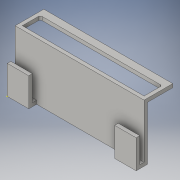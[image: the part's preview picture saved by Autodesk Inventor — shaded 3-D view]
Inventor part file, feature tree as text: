
AUTODESK INVENTOR PART (.ipt)
format: ipt  version: 2016 (Build 200138000, 138)  size: 142,336 bytes
history: native  units: in
note: dims shown in document units (in); Inventor stores cm internally (conversion verified against a paired STEP export)
features: sketch x4, extrude x3, projected_geometry x1
ambient origin geometry x8: Origin, YZ Plane, XZ Plane, XY Plane, X Axis, Y Axis, Z Axis, Center Point
bodies: Solid1 (feature_tree)
feature tree (8):
  sketch  "Sketch1"  dims[d0=4.0in d1=2.55in]
  sketch  "Sketch2"  dims[d2=3.75in d3=0.3in]
  extrude  "Extrusion1"  Depth=2.55in
  extrude  "Extrusion2"  Depth=0.3in
  extrude  "Extrusion3"  Depth=3.75in
  sketch  "Sketch3"  dims[d4=0.25in d5=3.75in]
  sketch  "Sketch4"  dims[d6=1.75in d7=2.0in d8=9.0in d9=0.0in d10=8.5in d11=1.25in d12=0.25in d13=0.125in d14=0.125in d17=9.0in d18=0.0in d19=8.5in d20=9.0in d21=0.0in d23=6.0in d24=0.55in d25=1.5in]
  projected_geometry  "Projected Loop1"
